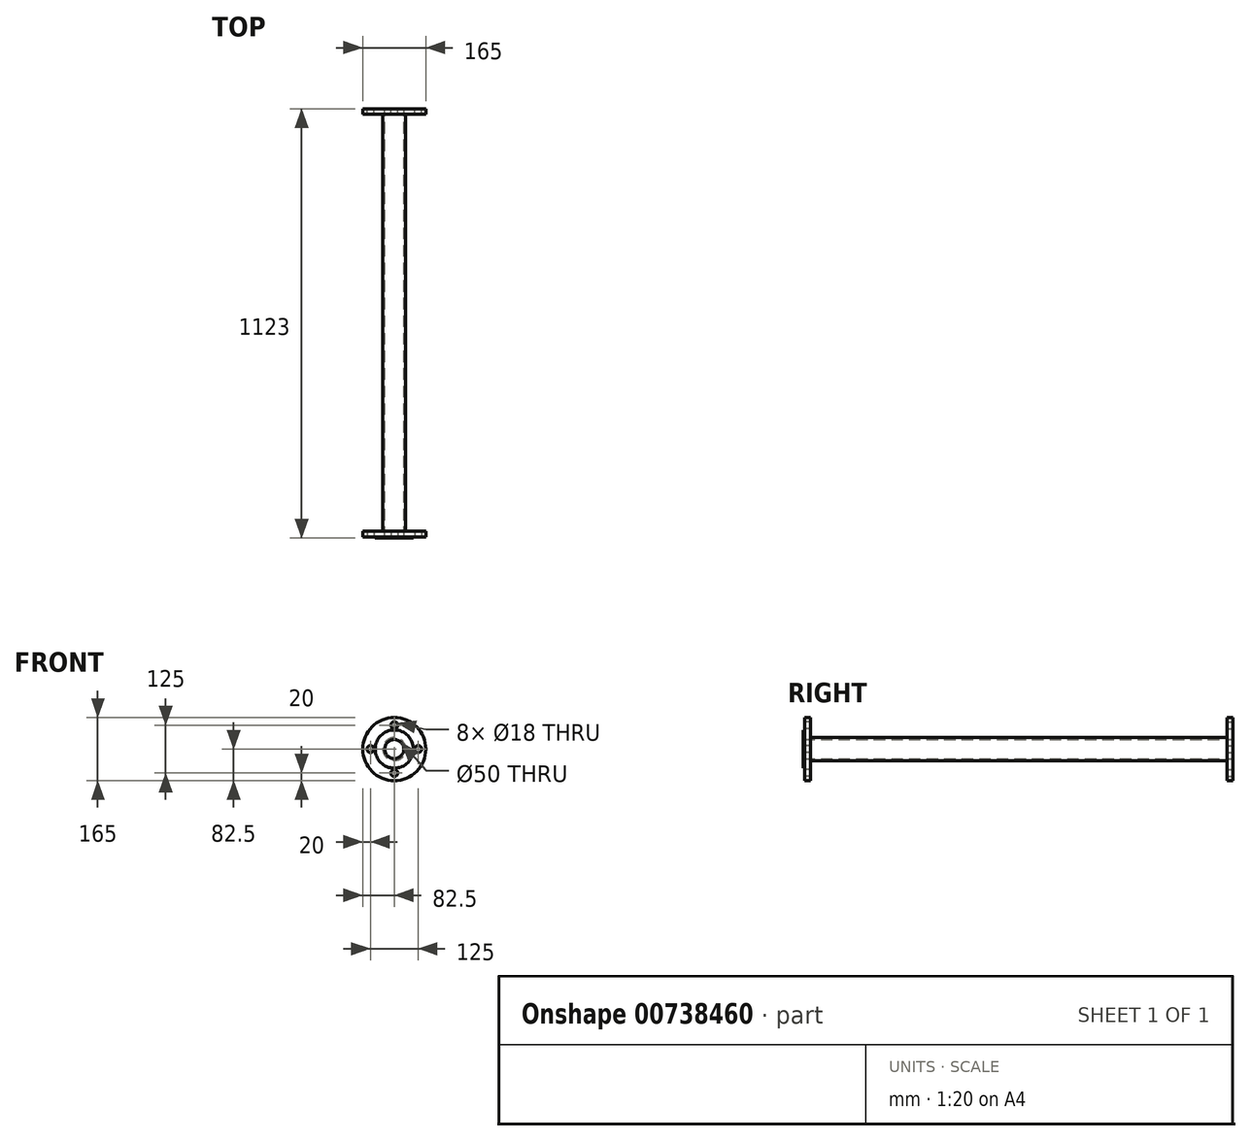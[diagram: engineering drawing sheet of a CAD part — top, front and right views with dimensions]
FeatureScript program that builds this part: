
annotation { "Feature Type Name" : "Feature", "Feature Type Description" : "" }
export const myFeature = defineFeature(function(context is Context, id is Id, definition is map)
    precondition{}
    {
        {
            var Q0;
            Q0=qCreatedBy(makeId("Front.planeOp"),FACE);
            var sketch = newSketch(context, id + "F0", { "sketchPlane" : qUnion([Q0])});
            skCircle(sketch, "E0", {"center": v(0, 0) * mm, "radius": 25 * mm});
            skCircle(sketch, "E1", {"center": v(0, 0) * mm, "radius": 30 * mm});
            skCircle(sketch, "E2", {"center": v(0, 0) * mm, "radius": 82.5 * mm});
            skCircle(sketch, "E3", {"center": v(0, 62.5) * mm, "radius": 9 * mm});
            skCircle(sketch, "E4.1.0", {"center": v(-62.5, 0) * mm, "radius": 9 * mm});
            skCircle(sketch, "E4.2.0", {"center": v(0, -62.5) * mm, "radius": 9 * mm});
            skCircle(sketch, "E4.3.0", {"center": v(62.5, 0) * mm, "radius": 9 * mm});
            skSolve(sketch);
        }
        {
            var Q0;
            Q0=makeQuery(id+"F0.imprint","IMPRINT",FACE,{"disambiguationData":[TD([[makeQuery(id+"F0.imprint","IMPRINT",EDGE,{"derivedFrom":sQuery(id+"F0.wireOp",EDGE,"E0")}),-1.0]])]});
            extrude(context, id + "F1", {"entities" : qUnion([Q0]), "depth" : 1120 * mm, "offsetDistance" : 25 * mm});
        }
        {
            var Q0;
            Q0=makeQuery(id+"F0.imprint","IMPRINT",FACE,{"disambiguationData":[TD([[makeQuery(id+"F0.imprint","IMPRINT",EDGE,{"derivedFrom":sQuery(id+"F0.wireOp",EDGE,"E1")}),-1.0]])]});
            extrude(context, id + "F2", {"entities" : qUnion([Q0]), "operationType" : NewBodyOperationType.ADD, "depth" : 15 * mm, "offsetDistance" : 25 * mm});
        }
        {
            var Q0;
            Q0=makeQuery(id+"F1.opExtrude","CAP_FACE",FACE,{"disambiguationData":[OSD([sQuery(id+"F0.wireOp",EDGE,"E0"),sQuery(id+"F0.wireOp",EDGE,"E1")])],"isStart":false});
            var sketch = newSketch(context, id + "F3", { "sketchPlane" : qUnion([Q0])});
            skCircle(sketch, "E5.0.0", {"center": v(0, 0) * mm, "radius": 82.5 * mm});
            skCircle(sketch, "E6.0.0", {"center": v(0, 62.5) * mm, "radius": 9 * mm});
            skCircle(sketch, "E7.0.0", {"center": v(62.5, 0) * mm, "radius": 9 * mm});
            skCircle(sketch, "E8.0.0", {"center": v(-62.5, 0) * mm, "radius": 9 * mm});
            skCircle(sketch, "E9.0", {"center": v(0, -62.5) * mm, "radius": 9 * mm});
            skSolve(sketch);
        }
        {
            var Q0;
            Q0=makeQuery(id+"F3.imprint","IMPRINT",FACE,{"disambiguationData":[TD([[makeQuery(id+"F3.imprint","IMPRINT",EDGE,{"derivedFrom":sQuery(id+"F3.wireOp",EDGE,"E5.0.0")}),1.0]])]});
            extrude(context, id + "F4", {"entities" : qUnion([Q0]), "operationType" : NewBodyOperationType.ADD, "oppositeDirection" : true, "depth" : 15 * mm, "offsetDistance" : 25 * mm});
        }
        {
            var Q0;
            {var subQ0=sQuery(id+"F0.wireOp",EDGE,"E1");Q0=makeQuery(id+"F4.boolean.opBoolean","MERGE",FACE,{"derivedFrom":[makeQuery(id+"F1.opExtrude","CAP_FACE",FACE,{"disambiguationData":[OSD([sQuery(id+"F0.wireOp",EDGE,"E0"),subQ0])],"isStart":false}),makeQuery(id+"F4.opExtrude","CAP_FACE",FACE,{"disambiguationData":[OSD([subQ0,sQuery(id+"F3.wireOp",EDGE,"E5.0.0"),sQuery(id+"F3.wireOp",EDGE,"E6.0.0"),sQuery(id+"F3.wireOp",EDGE,"E7.0.0"),sQuery(id+"F3.wireOp",EDGE,"E8.0.0"),sQuery(id+"F3.wireOp",EDGE,"E9.0")])],"isStart":true})]});}
            var sketch = newSketch(context, id + "F5", { "sketchPlane" : qUnion([Q0])});
            skCircle(sketch, "E10", {"center": v(0, 0) * mm, "radius": 50 * mm});
            skSolve(sketch);
        }
        {
            var Q0;
            Q0=makeQuery(id+"F5.imprint","IMPRINT",FACE,{"disambiguationData":[TD([[makeQuery(id+"F5.imprint","IMPRINT",EDGE,{"derivedFrom":sQuery(id+"F5.wireOp",EDGE,"E10")}),1.0]])]});
            extrude(context, id + "F6", {"entities" : qUnion([Q0]), "operationType" : NewBodyOperationType.ADD, "depth" : 3 * mm, "offsetDistance" : 25 * mm});
        }
    });
